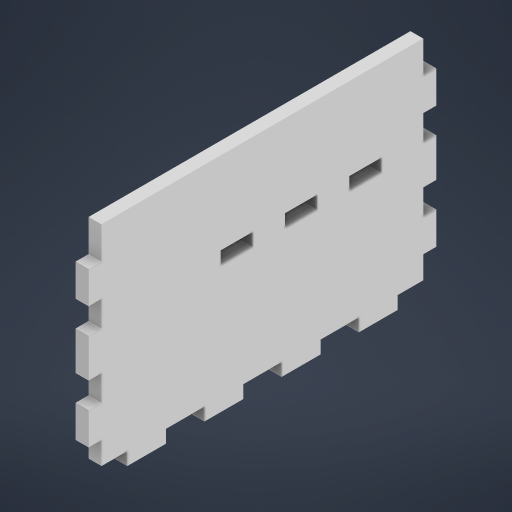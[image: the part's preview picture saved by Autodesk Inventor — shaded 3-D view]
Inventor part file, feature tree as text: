
AUTODESK INVENTOR PART (.ipt)
format: ipt  version: 2023.2 (Build 272271000, 271)  size: 314,368 bytes
history: native  units: mm
features: sketch x2
ambient origin geometry x8: Origin, YZ Plane, XZ Plane, XY Plane, X Axis, Y Axis, Z Axis, Center Point
bodies: Body1 (feature_tree)
feature tree (2):
  sketch  "Sketch1"  dims[d228=69.0mm]
  sketch  "Sketch3"  dims[d229=108.0mm d230=4.0mm d231=0.0mm d246=12.0mm d248=10.0mm d250=8.0mm d253=4.0mm d256=10.0mm d257=12.0mm d259=12.0mm d261=4.0mm d262=0.0mm d265=35.5mm d266=26.0mm d267=10.0mm d270=4.0mm d271=0.0mm d272=4.0mm d274=10.0mm d275=10.0mm d276=10.0mm d277=10.0mm d9=0.5mm d10=0.872665mm d11=0.5mm d12=0.872665mm d13=0.5mm d14=0.872665mm d27=0.5mm d28=0.872665mm d29=0.5mm d30=0.872665mm d88=0.5mm d89=0.872665mm d90=0.5mm d91=0.872665mm d116=0.5mm d117=0.872665mm d118=0.5mm d119=0.872665mm d154=0.5mm d155=0.872665mm d156=0.5mm d157=0.872665mm d181=0.5mm d182=0.872665mm d183=0.5mm d184=0.872665mm d221=0.5mm d222=0.872665mm d223=0.5mm d224=0.872665mm]
